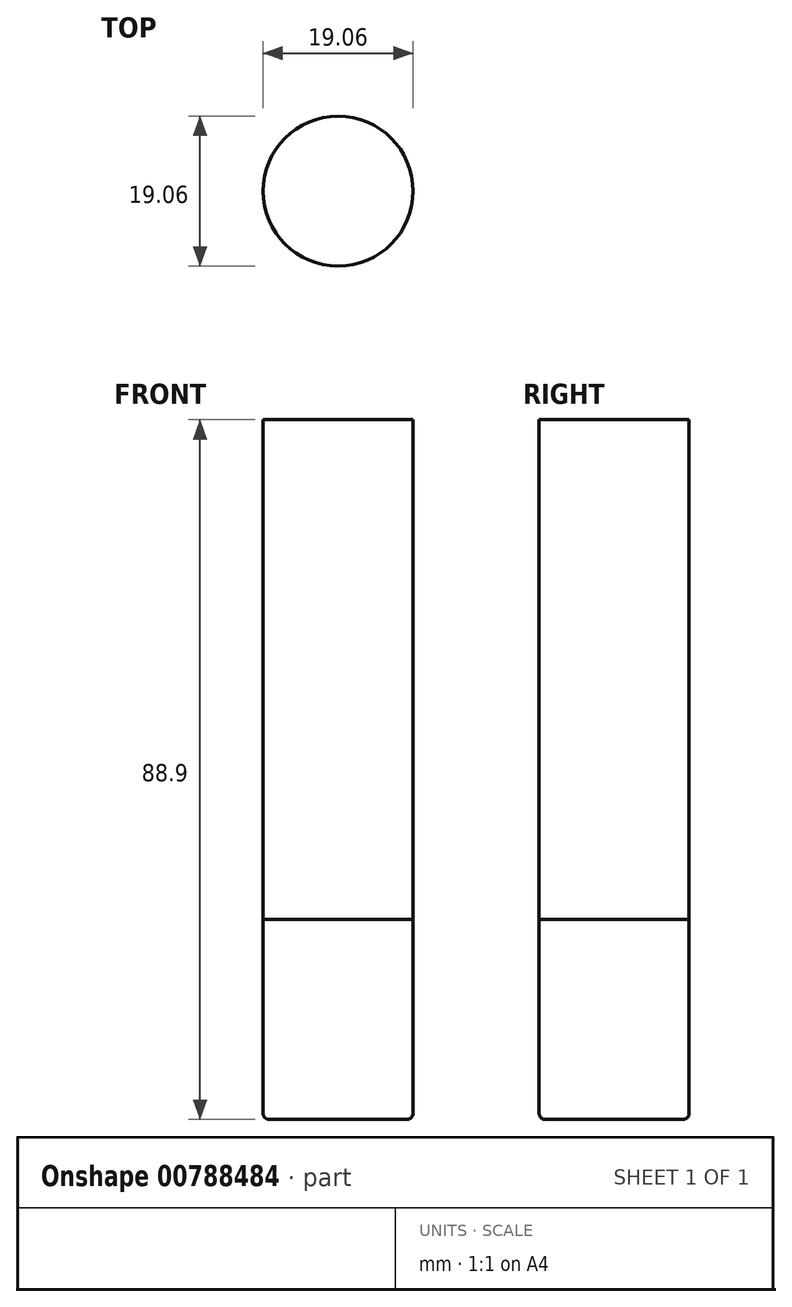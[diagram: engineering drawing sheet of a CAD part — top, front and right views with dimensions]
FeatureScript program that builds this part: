
annotation { "Feature Type Name" : "Feature", "Feature Type Description" : "" }
export const myFeature = defineFeature(function(context is Context, id is Id, definition is map)
    precondition{}
    {
        {
            var Q0;
            Q0=qCreatedBy(makeId("Front.planeOp"),FACE);
            var sketch = newSketch(context, id + "F0", { "sketchPlane" : qUnion([Q0])});
            skLineSegment(sketch, "E0", {"start": v(0, 0) * mm, "end": v(9.52, 0) * mm});
            skLineSegment(sketch, "E1", {"start": v(9.52, 0) * mm, "end": v(9.53, -88.14) * mm});
            skLineSegment(sketch, "E2", {"start": v(8.76, -88.9) * mm, "end": v(0, -88.9) * mm});
            skLineSegment(sketch, "E3", {"start": v(0, -88.9) * mm, "end": v(0, 0) * mm});
            skLineSegment(sketch, "E4", {"start": v(0, -63.5) * mm, "end": v(9.53, -63.5) * mm});
            skPoint(sketch, "E5.visualSharp", {"position": v(9.53, -88.9) * mm});
            skArc(sketch, "E5.filletArc", {"start": v(8.76, -88.9) * mm, "mid": v(9.3, -88.68) * mm, "end": v(9.53, -88.14) * mm});
            skSolve(sketch);
        }
        {
            var Q0;
            {var subQ0=sQuery(id+"F0.wireOp",EDGE,"E0");Q0=makeQuery(id+"F0.imprint","IMPRINT",FACE,{"disambiguationData":[TD([[makeQuery(id+"F0.imprint","IMPRINT",EDGE,{"derivedFrom":subQ0}),-1.0]])]});}
            var Q1;
            Q1=sQuery(id+"F0.wireOp",EDGE,"E3");
            revolve(context, id + "F1", {"entities" : qUnion([Q0]), "axis" : qUnion([Q1]), "revolveType" : RevolveType.FULL});
        }
        {
            var Q0;
            {var subQ2=sQuery(id+"F0.wireOp",EDGE,"E2");Q0=makeQuery(id+"F0.imprint","IMPRINT",FACE,{"disambiguationData":[TD([[makeQuery(id+"F0.imprint","IMPRINT",EDGE,{"derivedFrom":subQ2}),-1.0]])]});}
            var Q1;
            Q1=sQuery(id+"F0.wireOp",EDGE,"E3");
            revolve(context, id + "F2", {"entities" : qUnion([Q0]), "axis" : qUnion([Q1]), "revolveType" : RevolveType.FULL});
        }
    });
